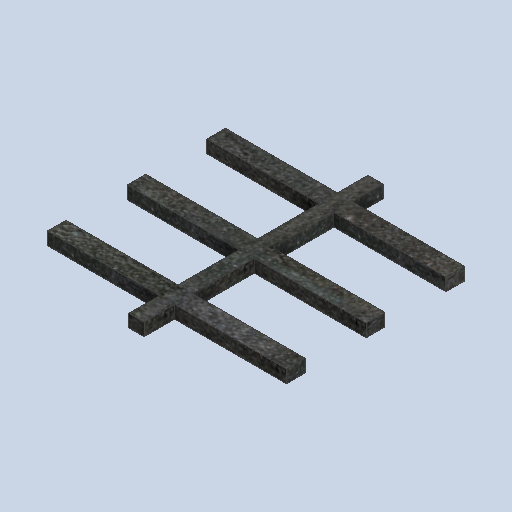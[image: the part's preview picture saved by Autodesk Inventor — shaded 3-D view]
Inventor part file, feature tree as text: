
AUTODESK INVENTOR PART (.ipt)
format: ipt  version: 2024.3 (Build 283343000, 343)  size: 270,336 bytes
history: native  units: mm
features: extrude x2, mirror x2, sketch x1
ambient origin geometry x8: Origin, YZ Plane, XZ Plane, XY Plane, X Axis, Y Axis, Z Axis, Center Point
bodies: Solid1 (feature_tree)
feature tree (5):
  sketch  "Sketch1"  dims[d0=94.0mm d1=94.0mm d2=12.0mm d3=24.0mm d4=7.333mm d5=5.0mm d6=0.0mm d7=5.0mm d8=0.0mm d9=3.0mm d10=0.0mm]
  extrude  "Extrusion1"  Depth=94.0mm
  extrude  "Extrusion2"  Depth=12.0mm
  mirror  "Mirror1"
  mirror  "Mirror2"
